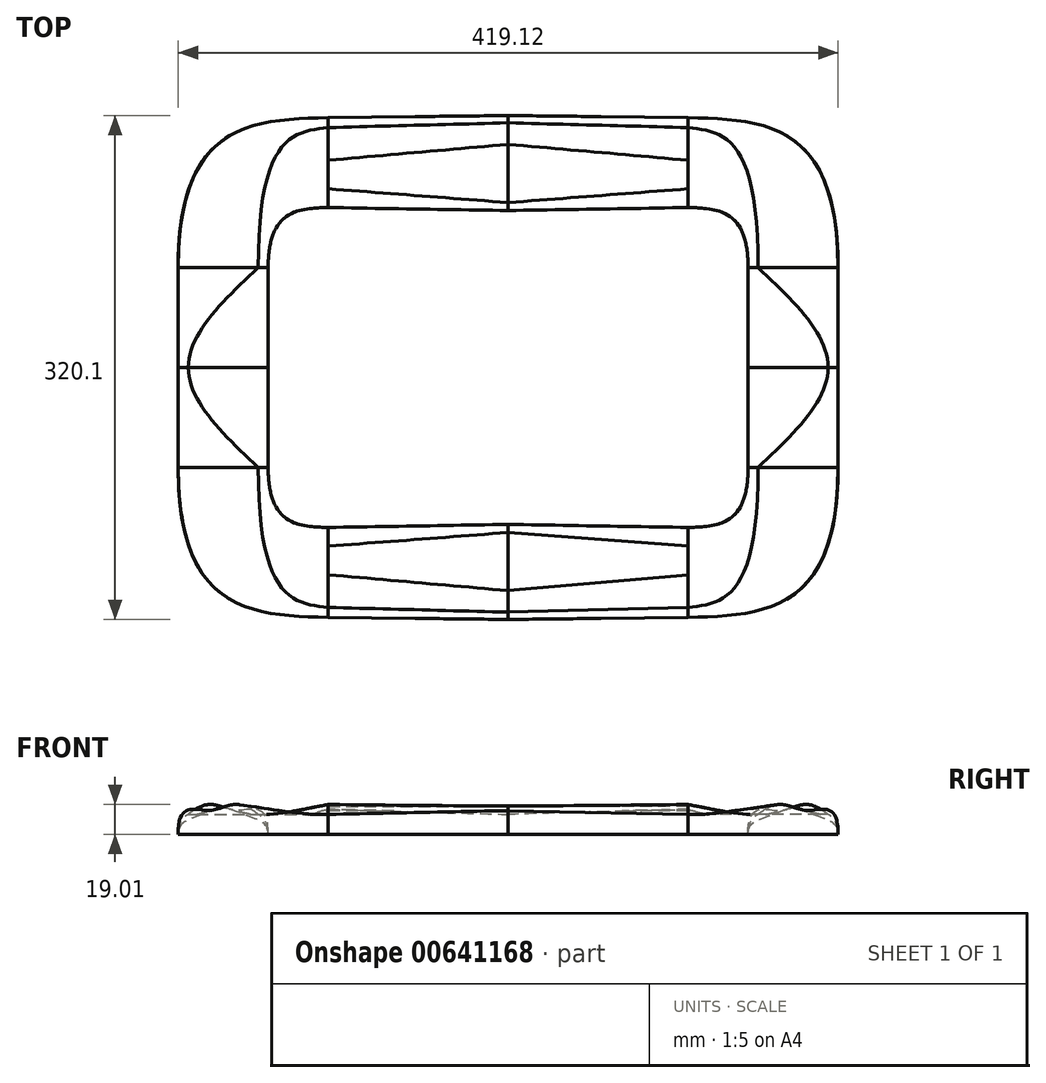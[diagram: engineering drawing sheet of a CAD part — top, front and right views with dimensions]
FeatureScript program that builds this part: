
annotation { "Feature Type Name" : "Feature", "Feature Type Description" : "" }
export const myFeature = defineFeature(function(context is Context, id is Id, definition is map)
    precondition{}
    {
        {
            var Q0;
            Q0=qCreatedBy(makeId("Top.planeOp"),FACE);
            var sketch = newSketch(context, id + "F0", { "sketchPlane" : qUnion([Q0])});
            skLineSegment(sketch, "E0.bottom", {"start": v(114.3, -101.6) * mm, "end": v(0, -101.6) * mm});
            skLineSegment(sketch, "E0.left", {"start": v(152.4, -63.5) * mm, "end": v(152.4, 0) * mm});
            skPoint(sketch, "E0.middle", {"position": v(0, 0) * mm});
            skPoint(sketch, "E1.visualSharp", {"position": v(152.4, -101.6) * mm});
            skArc(sketch, "E1.filletArc", {"start": v(114.3, -101.6) * mm, "mid": v(141.24, -90.44) * mm, "end": v(152.4, -63.5) * mm});
            skPoint(sketch, "E2.visualSharp", {"position": v(152.4, 101.6) * mm});
            skSolve(sketch);
        }
        {
            var Q0;
            Q0=qCreatedBy(makeId("Right.planeOp"),FACE);
            var sketch = newSketch(context, id + "F1", { "sketchPlane" : qUnion([Q0])});
            skLineSegment(sketch, "E3", {"start": v(-99.7, 0) * mm, "end": v(-160.02, 0) * mm});
            skArc(sketch, "E4", {"start": v(-141.73, 17.78) * mm, "mid": v(-148.8, 17.54) * mm, "end": v(-155.41, 15.07) * mm});
            skArc(sketch, "E5", {"start": v(-99.7, 0) * mm, "mid": v(-100.88, 6.9) * mm, "end": v(-104.78, 12.7) * mm});
            skFitSpline(sketch, "E6", {"points": [v(-104.78, 12.7) * mm, v(-141.73, 17.78) * mm], "startDerivative": vector(-7.4, 10.97) * mm, "endDerivative": vector(-26.3, 14.45) * mm});
            skPoint(sketch, "E7", {"position": v(-128.29, 15.1) * mm});
            skFitSpline(sketch, "E8", {"points": [v(-160.02, 0) * mm, v(-155.41, 15.07) * mm], "startDerivative": vector(-1.17, 19.73) * mm, "endDerivative": vector(4.88, 2.55) * mm});
            skSolve(sketch);
        }
        {
            var Q0;
            Q0=qCreatedBy(makeId("Front.planeOp"),FACE);
            var sketch = newSketch(context, id + "F2", { "sketchPlane" : qUnion([Q0])});
            skLineSegment(sketch, "E9", {"start": v(152.4, 0) * mm, "end": v(209.55, 0) * mm});
            skFitSpline(sketch, "E10", {"points": [v(152.4, 0) * mm, v(172.72, 15.24) * mm, v(203.2, 12.7) * mm], "startDerivative": vector(-2.66, 137.06) * mm, "endDerivative": vector(84.2, -70.25) * mm});
            skFitSpline(sketch, "E11", {"points": [v(209.55, 0) * mm, v(203.2, 12.7) * mm], "startDerivative": vector(-1.1, 16.32) * mm, "endDerivative": vector(-16.83, 9.39) * mm});
            skSolve(sketch);
        }
        {
            var Q0;
            Q0=sQuery(id+"F0.wireOp",VERTEX,"E1.filletArc.start");
            var Q1;
            Q1=sQuery(id+"F0.wireOp",EDGE,"E0.bottom");
            cPlane(context, id + "F3", {"entities" : qUnion([Q0, Q1]), "cplaneType" : CPlaneType.LINE_POINT, "offset" : 25.4 * mm, "width" : 152.4 * mm, "height" : 152.4 * mm});
        }
        {
            var Q0;
            Q0=qCreatedBy(id+"F3.planeOp",FACE);
            var sketch = newSketch(context, id + "F4", { "sketchPlane" : qUnion([Q0])});
            skLineSegment(sketch, "E12", {"start": v(101.6, 0) * mm, "end": v(158.75, 0) * mm});
            skFitSpline(sketch, "E13", {"points": [v(101.6, 0) * mm, v(121.92, 15.24) * mm, v(152.4, 12.7) * mm], "startDerivative": vector(-2.66, 137.06) * mm, "endDerivative": vector(84.2, -70.25) * mm});
            skFitSpline(sketch, "E14", {"points": [v(101.6, 0) * mm, v(121.92, 15.24) * mm, v(152.4, 12.7) * mm], "startDerivative": vector(-2.66, 137.06) * mm, "endDerivative": vector(84.2, -70.25) * mm});
            skFitSpline(sketch, "E15", {"points": [v(158.75, 0) * mm, v(152.4, 12.7) * mm], "startDerivative": vector(-1.1, 16.32) * mm, "endDerivative": vector(-16.83, 9.39) * mm});
            skSolve(sketch);
        }
        {
            var Q0;
            Q0=sQuery(id+"F0.wireOp",VERTEX,"E1.filletArc.end");
            var Q1;
            Q1=sQuery(id+"F0.wireOp",EDGE,"E0.left");
            cPlane(context, id + "F5", {"entities" : qUnion([Q0, Q1]), "cplaneType" : CPlaneType.LINE_POINT, "offset" : 25.4 * mm, "width" : 152.4 * mm, "height" : 152.4 * mm});
        }
        {
            var Q0;
            Q0=qCreatedBy(id+"F5.planeOp",FACE);
            var sketch = newSketch(context, id + "F6", { "sketchPlane" : qUnion([Q0])});
            skLineSegment(sketch, "E16", {"start": v(-209.55, 0) * mm, "end": v(-152.4, 0) * mm});
            skFitSpline(sketch, "E17", {"points": [v(-209.55, 0) * mm, v(-189.23, 15.24) * mm, v(-158.75, 12.7) * mm], "startDerivative": vector(-2.66, 137.06) * mm, "endDerivative": vector(84.2, -70.25) * mm});
            skFitSpline(sketch, "E18", {"points": [v(-152.4, 0) * mm, v(-158.75, 12.7) * mm], "startDerivative": vector(-1.1, 16.32) * mm, "endDerivative": vector(-16.83, 9.39) * mm});
            skSolve(sketch);
        }
        {
            var Q0;
            Q0=makeQuery(id+"F4.imprint","IMPRINT",FACE,{"disambiguationData":[TD([[makeQuery(id+"F4.imprint","IMPRINT",EDGE,{"derivedFrom":sQuery(id+"F4.wireOp",EDGE,"E12")}),1.0]])]});
            var Q1;
            Q1=makeQuery(id+"F1.imprint","IMPRINT",FACE,{"disambiguationData":[TD([[makeQuery(id+"F1.imprint","IMPRINT",EDGE,{"derivedFrom":sQuery(id+"F1.wireOp",EDGE,"E3")}),-1.0]])]});
            var Q2;
            Q2=sQuery(id+"F4.wireOp",VERTEX,"E15.start");
            var Q3;
            Q3=sQuery(id+"F1.wireOp",VERTEX,"E8.0.internal");
            loft(context, id + "F7", {"sheetProfilesArray" : [{ "sheetProfileEntities" : qUnion([Q0]) }, { "sheetProfileEntities" : qUnion([Q1]) }], "matchConnections" : true, "connections" : [{ "connectionEntities" : qUnion([Q2, Q3]), "connectionEdgeQueries" : qUnion([]), "connectionEdgeParameters" : [] }]});
        }
        {
            var Q0;
            Q0=makeQuery(id+"F2.imprint","IMPRINT",FACE,{"disambiguationData":[TD([[makeQuery(id+"F2.imprint","IMPRINT",EDGE,{"derivedFrom":sQuery(id+"F2.wireOp",EDGE,"E9")}),1.0]])]});
            var Q1;
            Q1=makeQuery(id+"F6.imprint","IMPRINT",FACE,{"disambiguationData":[TD([[makeQuery(id+"F6.imprint","IMPRINT",EDGE,{"derivedFrom":sQuery(id+"F6.wireOp",EDGE,"E16")}),1.0]])]});
            loft(context, id + "F8", {"startCondition" : LoftEndDerivativeType.NORMAL_TO_PROFILE, "startMagnitude" : 1, "sheetProfilesArray" : [{ "sheetProfileEntities" : qUnion([Q0]) }, { "sheetProfileEntities" : qUnion([Q1]) }]});
        }
        {
            var Q1;
            Q1=makeQuery(id+"F8.opLoft","CAP_FACE",FACE,{"disambiguationData":[OSD([makeQuery(id+"F6.imprint","IMPRINT",FACE,{"disambiguationData":[TD([[makeQuery(id+"F6.imprint","IMPRINT",EDGE,{"derivedFrom":sQuery(id+"F6.wireOp",EDGE,"E16")}),1.0]])]})])],"isStart":true});
            var Q2;
            Q2=makeQuery(id+"F4.imprint","IMPRINT",FACE,{"disambiguationData":[TD([[makeQuery(id+"F4.imprint","IMPRINT",EDGE,{"derivedFrom":sQuery(id+"F4.wireOp",EDGE,"E12")}),1.0]])]});
            var Q3;
            Q3=sQuery(id+"F0.wireOp",EDGE,"E1.filletArc");
            loft(context, id + "F9", {"operationType" : NewBodyOperationType.ADD, "startCondition" : LoftEndDerivativeType.NORMAL_TO_PROFILE, "startMagnitude" : 2.8, "sheetProfilesArray" : [{ "sheetProfileEntities" : qUnion([Q1]) }, { "sheetProfileEntities" : qUnion([Q2]) }], "guidesArray" : [{ "guideEntities" : qUnion([Q3]), "guideDerivativeType" : LoftGuideDerivativeType.DEFAULT, "guideDerivativeMagnitude" : 1 }]});
        }
        {
            var Q0;
            Q0=makeQuery(id+"F7.opLoft","SWEPT_BODY",BODY,{"disambiguationData":[OSD([makeQuery(id+"F1.imprint","IMPRINT",FACE,{"disambiguationData":[TD([[makeQuery(id+"F1.imprint","IMPRINT",EDGE,{"derivedFrom":sQuery(id+"F1.wireOp",EDGE,"E3")}),-1.0]])]}),makeQuery(id+"F4.imprint","IMPRINT",FACE,{"disambiguationData":[TD([[makeQuery(id+"F4.imprint","IMPRINT",EDGE,{"derivedFrom":sQuery(id+"F4.wireOp",EDGE,"E12")}),1.0]])]})])]});
            var Q1;
            Q1=makeQuery(id+"F8.opLoft","SWEPT_BODY",BODY,{"disambiguationData":[OSD([makeQuery(id+"F2.imprint","IMPRINT",FACE,{"disambiguationData":[TD([[makeQuery(id+"F2.imprint","IMPRINT",EDGE,{"derivedFrom":sQuery(id+"F2.wireOp",EDGE,"E9")}),1.0]])]}),makeQuery(id+"F6.imprint","IMPRINT",FACE,{"disambiguationData":[TD([[makeQuery(id+"F6.imprint","IMPRINT",EDGE,{"derivedFrom":sQuery(id+"F6.wireOp",EDGE,"E16")}),1.0]])]})])]});
            var Q2;
            Q2=qCreatedBy(makeId("Right.planeOp"),FACE);
            mirror(context, id + "F10", {"operationType" : NewBodyOperationType.ADD, "entities" : qUnion([Q0, Q1]), "mirrorPlane" : qUnion([Q2])});
        }
        {
            var Q0;
            Q0=makeQuery(id+"F7.opLoft","SWEPT_BODY",BODY,{"disambiguationData":[OSD([makeQuery(id+"F1.imprint","IMPRINT",FACE,{"disambiguationData":[TD([[makeQuery(id+"F1.imprint","IMPRINT",EDGE,{"derivedFrom":sQuery(id+"F1.wireOp",EDGE,"E3")}),-1.0]])]}),makeQuery(id+"F4.imprint","IMPRINT",FACE,{"disambiguationData":[TD([[makeQuery(id+"F4.imprint","IMPRINT",EDGE,{"derivedFrom":sQuery(id+"F4.wireOp",EDGE,"E12")}),1.0]])]})])]});
            var Q1;
            Q1=makeQuery(id+"F8.opLoft","SWEPT_BODY",BODY,{"disambiguationData":[OSD([makeQuery(id+"F2.imprint","IMPRINT",FACE,{"disambiguationData":[TD([[makeQuery(id+"F2.imprint","IMPRINT",EDGE,{"derivedFrom":sQuery(id+"F2.wireOp",EDGE,"E9")}),1.0]])]}),makeQuery(id+"F6.imprint","IMPRINT",FACE,{"disambiguationData":[TD([[makeQuery(id+"F6.imprint","IMPRINT",EDGE,{"derivedFrom":sQuery(id+"F6.wireOp",EDGE,"E16")}),1.0]])]})])]});
            var Q2;
            Q2=qCreatedBy(makeId("Front.planeOp"),FACE);
            mirror(context, id + "F11", {"entities" : qUnion([Q0, Q1]), "mirrorPlane" : qUnion([Q2])});
        }
    });
